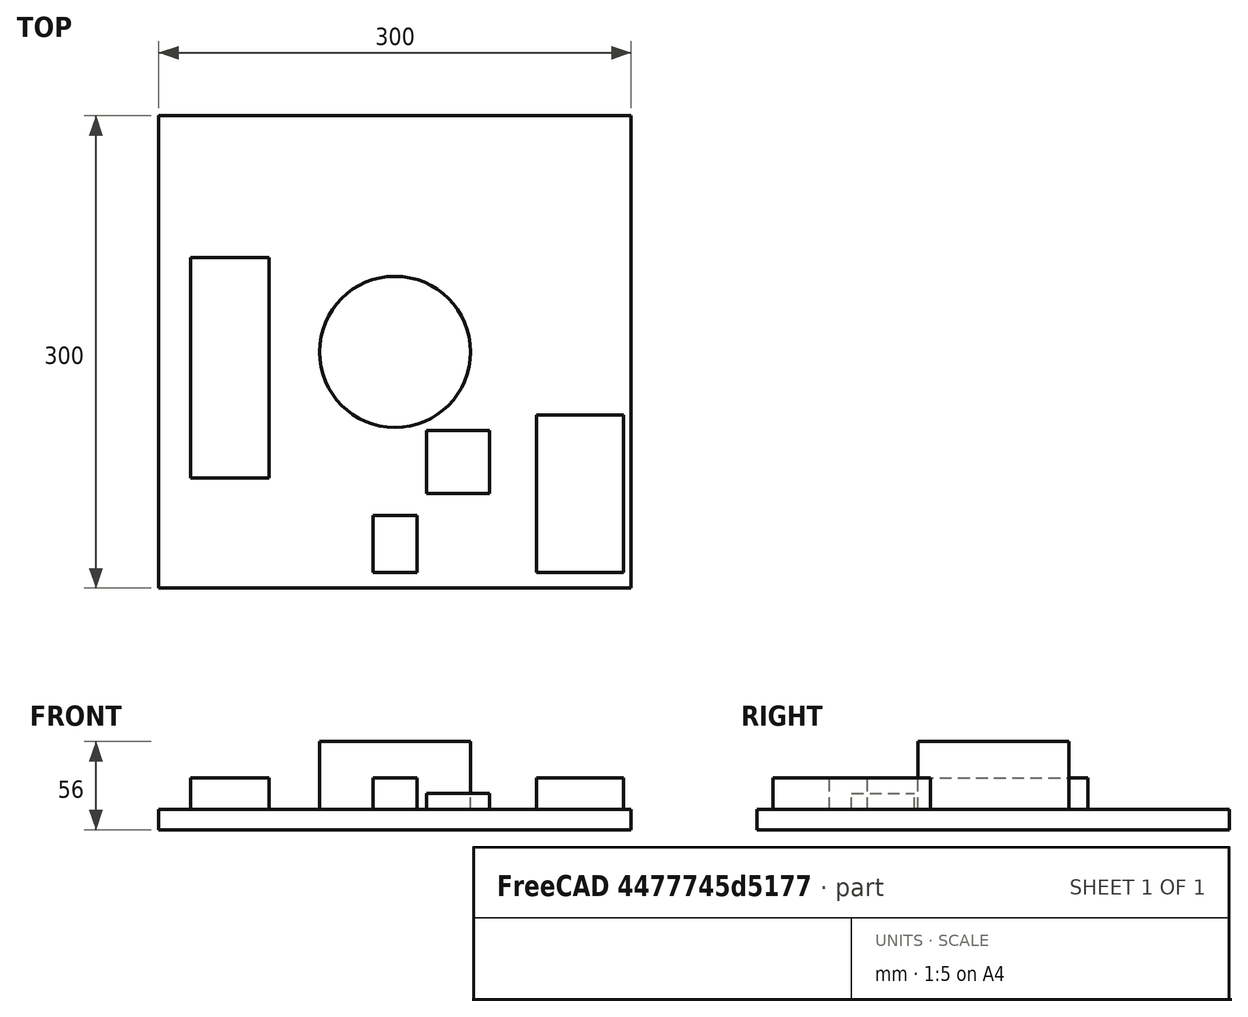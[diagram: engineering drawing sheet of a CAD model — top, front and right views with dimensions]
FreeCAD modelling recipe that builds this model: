
FCSTD DOCUMENT
Label: Base
objects: Part::Box×5, Part::Cylinder×1, Part::MultiFuse×1
note: 7 computed .brp shape members not serialized (recipe doc carries the construction recipe); baked Part::Feature solids carry a one-line shape summary decoded from their .brp

FEATURE [Part::Box] Box
  Height = 13
  Length = 300
  Width = 300
FEATURE [Part::Cylinder] Cylinder
  Angle = 360
  Height = 43
  Placement = pos=(150,150,13) rot=(0,0,1;0rad)
  Radius = 48
FEATURE [Part::Box] Box001  label="Battery"
  Height = 20
  Length = 50
  Placement = pos=(20,70,13) rot=(0,0,1;0rad)
  Width = 140
FEATURE [Part::Box] Box002  label="Arduino"
  Height = 20
  Length = 55
  Placement = pos=(240,10,13) rot=(0,0,1;0rad)
  Width = 100
FEATURE [Part::Box] Box003  label="Maestro"
  Height = 20
  Length = 28
  Placement = pos=(136,10,13) rot=(0,0,1;0rad)
  Width = 36
FEATURE [Part::Box] Box004  label="UBEC"
  Height = 10
  Length = 40
  Placement = pos=(170,60,13) rot=(0,0,1;0rad)
  Width = 40
FEATURE [Part::MultiFuse] Fusion  label="Base"
  Shapes = -> [Box,Cylinder,Box001,Box002,Box003,Box004]
